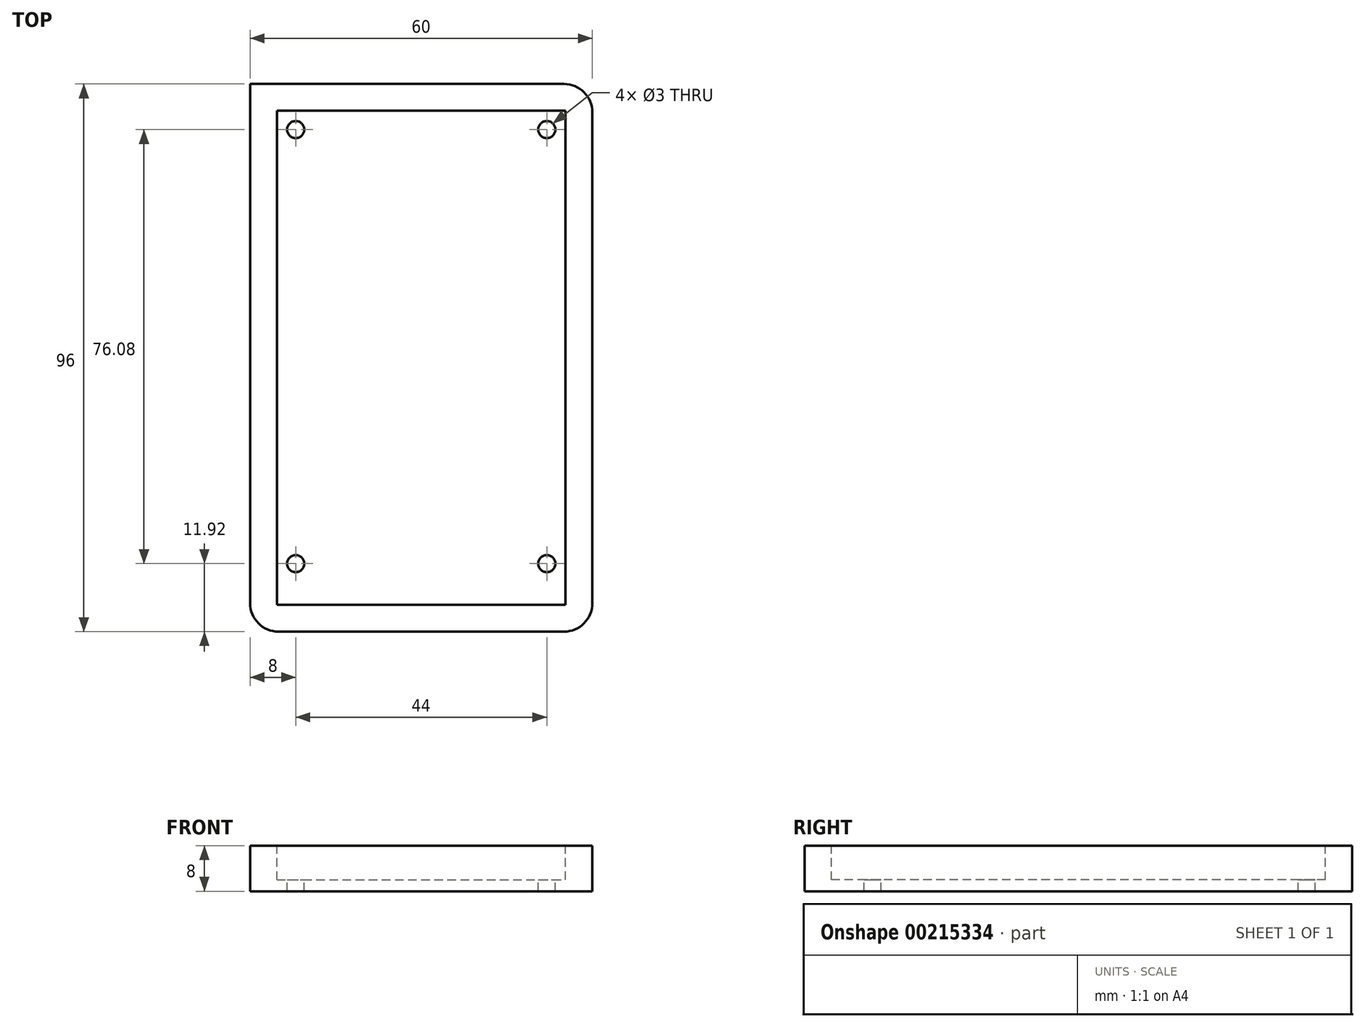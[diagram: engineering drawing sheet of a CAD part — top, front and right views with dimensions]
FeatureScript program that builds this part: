
annotation { "Feature Type Name" : "Feature", "Feature Type Description" : "" }
export const myFeature = defineFeature(function(context is Context, id is Id, definition is map)
    precondition{}
    {
        {
            var Q0;
            Q0=qCreatedBy(makeId("Top.planeOp"),FACE);
            var sketch = newSketch(context, id + "F0", { "sketchPlane" : qUnion([Q0])});
            skPoint(sketch, "E0.middle", {"position": v(0, 0) * mm});
            skCircle(sketch, "E1", {"center": v(-22, 40) * mm, "radius": 1.5 * mm});
            skCircle(sketch, "E2", {"center": v(22, 40) * mm, "radius": 1.5 * mm});
            skCircle(sketch, "E3", {"center": v(-22, -36.08) * mm, "radius": 1.5 * mm});
            skCircle(sketch, "E4", {"center": v(22, -36.08) * mm, "radius": 1.5 * mm});
            skLineSegment(sketch, "E5.bottom", {"start": v(25, -48) * mm, "end": v(-25, -48) * mm});
            skLineSegment(sketch, "E5.top", {"start": v(25, 48) * mm, "end": v(-27, 48) * mm});
            skLineSegment(sketch, "E5.left", {"start": v(30, -43) * mm, "end": v(30, 43) * mm});
            skLineSegment(sketch, "E5.right", {"start": v(-30, -43) * mm, "end": v(-30, 43) * mm});
            skPoint(sketch, "E6.visualSharp", {"position": v(-30, 48) * mm});
            skPoint(sketch, "E7.visualSharp", {"position": v(30, 48) * mm});
            skLineSegment(sketch, "E8.top", {"start": v(-30, 48) * mm, "end": v(-27, 48) * mm});
            skLineSegment(sketch, "E8.left", {"start": v(-30, 43) * mm, "end": v(-30, 48) * mm});
            skArc(sketch, "E9.filletArc", {"start": v(30, 43) * mm, "mid": v(28.54, 46.54) * mm, "end": v(25, 48) * mm});
            skPoint(sketch, "E10.visualSharp", {"position": v(30, -48) * mm});
            skArc(sketch, "E10.filletArc", {"start": v(25, -48) * mm, "mid": v(28.54, -46.54) * mm, "end": v(30, -43) * mm});
            skPoint(sketch, "E11.visualSharp", {"position": v(-30, -48) * mm});
            skArc(sketch, "E11.filletArc", {"start": v(-30, -43) * mm, "mid": v(-28.54, -46.54) * mm, "end": v(-25, -48) * mm});
            skSolve(sketch);
        }
        {
            var Q0;
            Q0=qSketchRegion(id+"F0",true);
            extrude(context, id + "F1", {"entities" : qUnion([Q0]), "depth" : 6 * mm});
        }
        {
            var Q0;
            Q0=makeQuery(id+"F1.opExtrude","CAP_FACE",FACE,{"disambiguationData":[OSD([sQuery(id+"F0.wireOp",EDGE,"E1"),sQuery(id+"F0.wireOp",EDGE,"E2"),sQuery(id+"F0.wireOp",EDGE,"E3"),sQuery(id+"F0.wireOp",EDGE,"E4"),sQuery(id+"F0.wireOp",EDGE,"E5.bottom"),sQuery(id+"F0.wireOp",EDGE,"E5.top"),sQuery(id+"F0.wireOp",EDGE,"E5.left"),sQuery(id+"F0.wireOp",EDGE,"E5.right")])],"isStart":false});
            var sketch = newSketch(context, id + "F2", { "sketchPlane" : qUnion([Q0])});
            skLineSegment(sketch, "E12.bottom", {"start": v(-25.3, 43.3) * mm, "end": v(25.3, 43.3) * mm});
            skLineSegment(sketch, "E12.top", {"start": v(-25.3, -43.3) * mm, "end": v(25.3, -43.3) * mm});
            skLineSegment(sketch, "E12.left", {"start": v(-25.3, 43.3) * mm, "end": v(-25.3, -43.3) * mm});
            skLineSegment(sketch, "E12.right", {"start": v(25.3, 43.3) * mm, "end": v(25.3, -43.3) * mm});
            skPoint(sketch, "E12.middle", {"position": v(0, 0) * mm});
            skCircle(sketch, "E13", {"center": v(-22, 40) * mm, "radius": 1.5 * mm});
            skCircle(sketch, "E14", {"center": v(22, 40) * mm, "radius": 1.5 * mm});
            skCircle(sketch, "E15", {"center": v(-22, -36.08) * mm, "radius": 1.5 * mm});
            skCircle(sketch, "E16", {"center": v(22, -36.08) * mm, "radius": 1.5 * mm});
            skSolve(sketch);
        }
        {
            var Q0;
            Q0=qSketchRegion(id+"F2",true);
            extrude(context, id + "F3", {"entities" : qUnion([Q0]), "operationType" : NewBodyOperationType.REMOVE, "oppositeDirection" : true, "depth" : 6 * mm});
        }
        {
            var Q0;
            Q0=makeQuery(id+"F1FxArUZZdRu1UE_1.boolean.opBoolean","MERGE",FACE,{"derivedFrom":[makeQuery(id+"F1.opExtrude","CAP_FACE",FACE,{"disambiguationData":[OSD([sQuery(id+"F0.wireOp",EDGE,"E1"),sQuery(id+"F0.wireOp",EDGE,"E2"),sQuery(id+"F0.wireOp",EDGE,"E3"),sQuery(id+"F0.wireOp",EDGE,"E4"),sQuery(id+"F0.wireOp",EDGE,"E5.bottom"),sQuery(id+"F0.wireOp",EDGE,"E5.top"),sQuery(id+"F0.wireOp",EDGE,"E5.left"),sQuery(id+"F0.wireOp",EDGE,"E5.right"),sQuery(id+"F0.wireOp",EDGE,"E8.top"),sQuery(id+"F0.wireOp",EDGE,"E8.left"),sQuery(id+"F0.wireOp",EDGE,"E9.filletArc"),sQuery(id+"F0.wireOp",EDGE,"E10.filletArc"),sQuery(id+"F0.wireOp",EDGE,"E11.filletArc")])],"isStart":true}),makeQuery(id+"F1FxArUZZdRu1UE_1.opExtrude","CAP_FACE",FACE,{"disambiguationData":[OSD([sQuery(id+"FJSclEh4idDcqSA_1.wireOp",EDGE,"84751b70-7844-4b05-870a-e177ed256b28"),sQuery(id+"FJSclEh4idDcqSA_1.wireOp",EDGE,"fVbu1CYc-aZui-lMua-0o8Y-0rwBd4JuUzI8.bottom"),sQuery(id+"FJSclEh4idDcqSA_1.wireOp",EDGE,"fVbu1CYc-aZui-lMua-0o8Y-0rwBd4JuUzI8.top"),sQuery(id+"FJSclEh4idDcqSA_1.wireOp",EDGE,"fVbu1CYc-aZui-lMua-0o8Y-0rwBd4JuUzI8.left"),sQuery(id+"FJSclEh4idDcqSA_1.wireOp",EDGE,"fVbu1CYc-aZui-lMua-0o8Y-0rwBd4JuUzI8.right"),sQuery(id+"FJSclEh4idDcqSA_1.wireOp",EDGE,"5b2c45bc-a8d7-4074-9361-63369f59a909.filletArc")])],"isStart":false}),makeQuery(id+"F1FxArUZZdRu1UE_1.opExtrude","CAP_FACE",FACE,{"disambiguationData":[OSD([sQuery(id+"FJSclEh4idDcqSA_1.wireOp",EDGE,"ecf71cdc-cb11-4dff-b2c5-2f1d65bab188"),sQuery(id+"FJSclEh4idDcqSA_1.wireOp",EDGE,"OP5LftRj-U8tE-vx9v-37I4-AzJBfcoGkHdH.bottom"),sQuery(id+"FJSclEh4idDcqSA_1.wireOp",EDGE,"OP5LftRj-U8tE-vx9v-37I4-AzJBfcoGkHdH.top"),sQuery(id+"FJSclEh4idDcqSA_1.wireOp",EDGE,"OP5LftRj-U8tE-vx9v-37I4-AzJBfcoGkHdH.left"),sQuery(id+"FJSclEh4idDcqSA_1.wireOp",EDGE,"OP5LftRj-U8tE-vx9v-37I4-AzJBfcoGkHdH.right"),sQuery(id+"FJSclEh4idDcqSA_1.wireOp",EDGE,"2f9e2e53-a408-45a8-97da-503b7f741175.filletArc")])],"isStart":false}),makeQuery(id+"F1FxArUZZdRu1UE_1.opExtrude","CAP_FACE",FACE,{"disambiguationData":[OSD([sQuery(id+"FJSclEh4idDcqSA_1.wireOp",EDGE,"0fa71abb-2216-4727-816d-04805a56cc04"),sQuery(id+"FJSclEh4idDcqSA_1.wireOp",EDGE,"DLAZhJWB-CZD5-HWjO-bbGw-RO5w4IXBKPv7.bottom"),sQuery(id+"FJSclEh4idDcqSA_1.wireOp",EDGE,"DLAZhJWB-CZD5-HWjO-bbGw-RO5w4IXBKPv7.top"),sQuery(id+"FJSclEh4idDcqSA_1.wireOp",EDGE,"DLAZhJWB-CZD5-HWjO-bbGw-RO5w4IXBKPv7.left"),sQuery(id+"FJSclEh4idDcqSA_1.wireOp",EDGE,"DLAZhJWB-CZD5-HWjO-bbGw-RO5w4IXBKPv7.right"),sQuery(id+"FJSclEh4idDcqSA_1.wireOp",EDGE,"72694baa-c404-4531-b296-8690fde29edc.filletArc")])],"isStart":false}),makeQuery(id+"F1FxArUZZdRu1UE_1.opExtrude","CAP_FACE",FACE,{"disambiguationData":[OSD([sQuery(id+"FJSclEh4idDcqSA_1.wireOp",EDGE,"M547aIjE-pOFM-Uavv-71df-CZgJttJAnNUW"),sQuery(id+"FJSclEh4idDcqSA_1.wireOp",EDGE,"iyk4e3wZ-THgz-imgX-eQSz-kuoQJS2Y4U6d.bottom"),sQuery(id+"FJSclEh4idDcqSA_1.wireOp",EDGE,"iyk4e3wZ-THgz-imgX-eQSz-kuoQJS2Y4U6d.top"),sQuery(id+"FJSclEh4idDcqSA_1.wireOp",EDGE,"iyk4e3wZ-THgz-imgX-eQSz-kuoQJS2Y4U6d.left"),sQuery(id+"FJSclEh4idDcqSA_1.wireOp",EDGE,"iyk4e3wZ-THgz-imgX-eQSz-kuoQJS2Y4U6d.right"),sQuery(id+"FJSclEh4idDcqSA_1.wireOp",EDGE,"8d05bdd5-a552-43bb-a48b-f247ab5198fe.filletArc")])],"isStart":false})]});
            var sketch = newSketch(context, id + "F4", { "sketchPlane" : qUnion([Q0])});
            skLineSegment(sketch, "E17.bottom", {"start": v(-30, -48) * mm, "end": v(25, -48) * mm});
            skLineSegment(sketch, "E17.top", {"start": v(-25, 48) * mm, "end": v(25, 48) * mm});
            skLineSegment(sketch, "E17.left", {"start": v(-30, -48) * mm, "end": v(-30, 43) * mm});
            skLineSegment(sketch, "E17.right", {"start": v(30, -43) * mm, "end": v(30, 43) * mm});
            skPoint(sketch, "E17.middle", {"position": v(0, 0) * mm});
            skPoint(sketch, "E18.visualSharp", {"position": v(-30, 48) * mm});
            skArc(sketch, "E18.filletArc", {"start": v(-25, 48) * mm, "mid": v(-28.54, 46.54) * mm, "end": v(-30, 43) * mm});
            skPoint(sketch, "E19.visualSharp", {"position": v(30, 48) * mm});
            skArc(sketch, "E19.filletArc", {"start": v(30, 43) * mm, "mid": v(28.54, 46.54) * mm, "end": v(25, 48) * mm});
            skPoint(sketch, "E20.visualSharp", {"position": v(30, -48) * mm});
            skArc(sketch, "E20.filletArc", {"start": v(25, -48) * mm, "mid": v(28.54, -46.54) * mm, "end": v(30, -43) * mm});
            skCircle(sketch, "E21", {"center": v(-22, 36.08) * mm, "radius": 1.5 * mm});
            skCircle(sketch, "E22", {"center": v(22, 36.08) * mm, "radius": 1.5 * mm});
            skCircle(sketch, "E23", {"center": v(22, -40) * mm, "radius": 1.5 * mm});
            skCircle(sketch, "E24", {"center": v(-22, -40) * mm, "radius": 1.5 * mm});
            skSolve(sketch);
        }
        {
            var Q0;
            Q0 = qSketchRegion(id + "F4", true);
            extrude(context, id + "F5", {"entities" : qUnion([Q0]), "operationType" : NewBodyOperationType.ADD, "depth" : 2 * mm});
        }
    });
